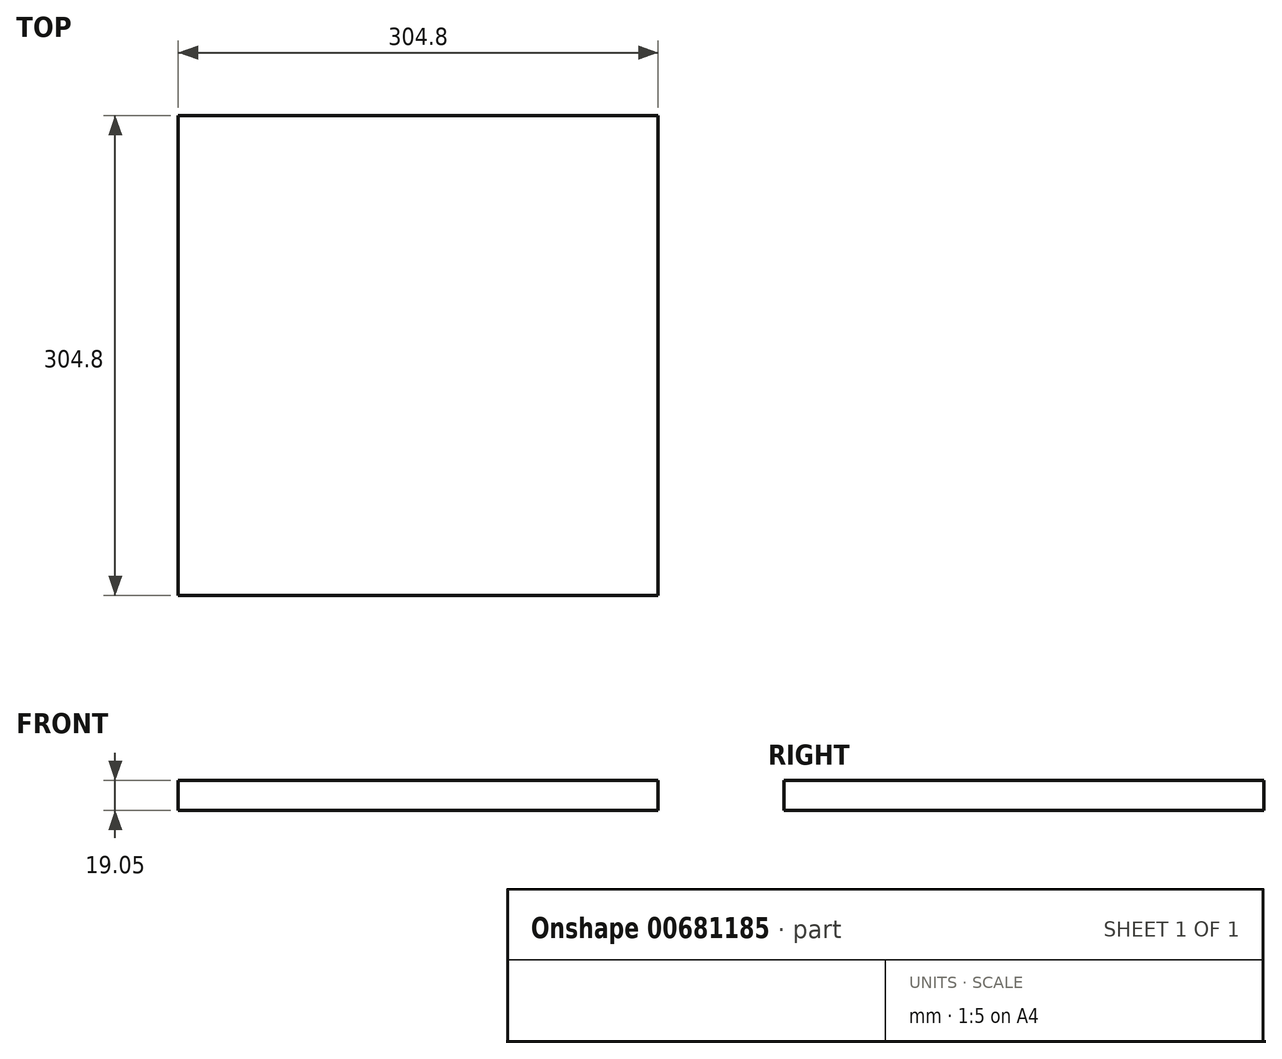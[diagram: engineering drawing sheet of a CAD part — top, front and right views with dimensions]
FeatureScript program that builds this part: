
annotation { "Feature Type Name" : "Feature", "Feature Type Description" : "" }
export const myFeature = defineFeature(function(context is Context, id is Id, definition is map)
    precondition{}
    {
        {
            var Q0;
            Q0=qCreatedBy(makeId("Top.planeOp"),FACE);
            var sketch = newSketch(context, id + "F0", { "sketchPlane" : qUnion([Q0])});
            skLineSegment(sketch, "E0.bottom", {"start": v(-152.4, 152.4) * mm, "end": v(152.4, 152.4) * mm});
            skLineSegment(sketch, "E0.top", {"start": v(-152.4, -152.4) * mm, "end": v(152.4, -152.4) * mm});
            skLineSegment(sketch, "E0.left", {"start": v(-152.4, 152.4) * mm, "end": v(-152.4, -152.4) * mm});
            skLineSegment(sketch, "E0.right", {"start": v(152.4, 152.4) * mm, "end": v(152.4, -152.4) * mm});
            skPoint(sketch, "E0.middle", {"position": v(0, 0) * mm});
            skSolve(sketch);
        }
        {
            var Q0;
            Q0=makeQuery(id+"F0.imprint","IMPRINT",FACE,{"disambiguationData":[TD([[makeQuery(id+"F0.imprint","IMPRINT",EDGE,{"derivedFrom":sQuery(id+"F0.wireOp",EDGE,"E0.bottom")}),-1.0]])]});
            extrude(context, id + "F1", {"entities" : qUnion([Q0]), "depth" : 19.05 * mm, "offsetDistance" : 25.4 * mm});
        }
    });
